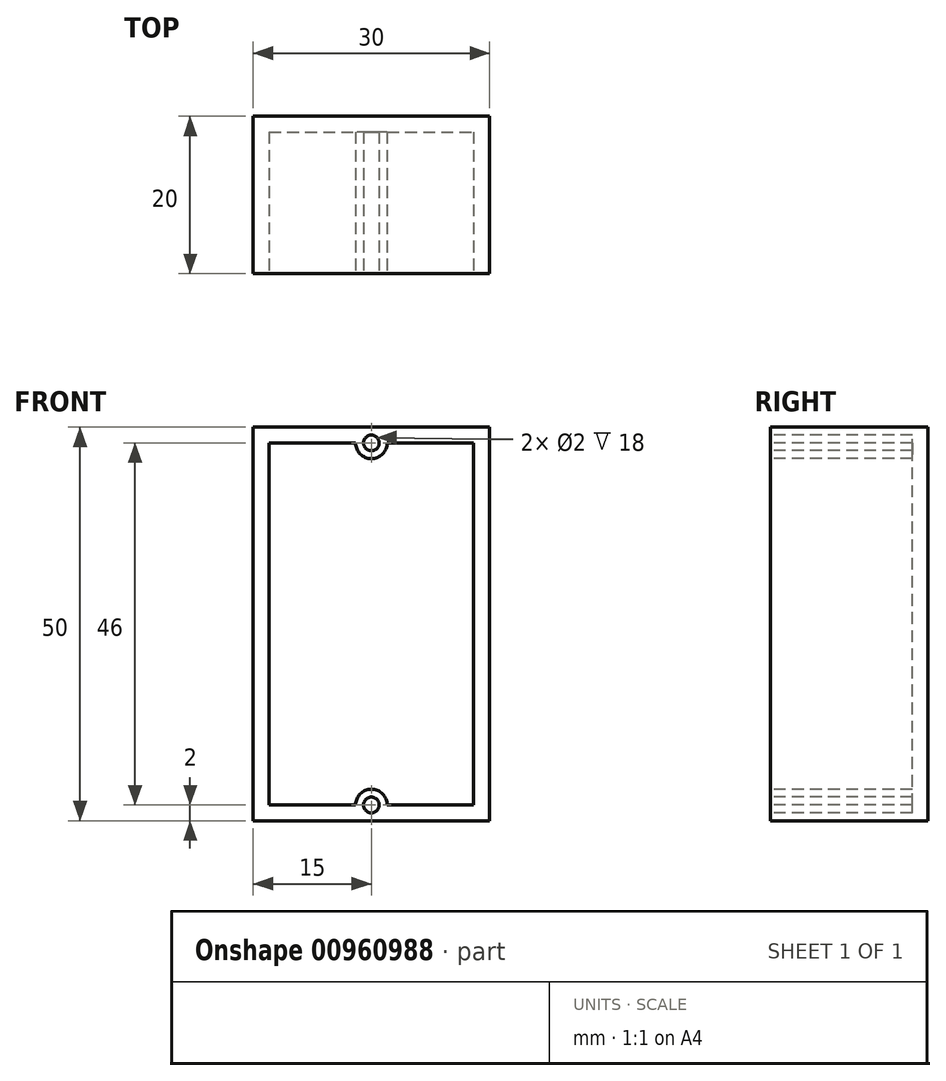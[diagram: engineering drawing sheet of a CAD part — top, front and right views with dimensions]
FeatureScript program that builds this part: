
annotation { "Feature Type Name" : "Feature", "Feature Type Description" : "" }
export const myFeature = defineFeature(function(context is Context, id is Id, definition is map)
    precondition{}
    {
        {
            var Q0;
            Q0=qCreatedBy(makeId("Front.planeOp"),FACE);
            var sketch = newSketch(context, id + "F0", { "sketchPlane" : qUnion([Q0])});
            skLineSegment(sketch, "E0.bottom", {"start": v(0, 0) * mm, "end": v(30, 0) * mm});
            skLineSegment(sketch, "E0.top", {"start": v(0, 50) * mm, "end": v(30, 50) * mm});
            skLineSegment(sketch, "E0.left", {"start": v(0, 0) * mm, "end": v(0, 50) * mm});
            skLineSegment(sketch, "E0.right", {"start": v(30, 0) * mm, "end": v(30, 50) * mm});
            skSolve(sketch);
        }
        {
            var Q0;
            Q0 = qSketchRegion(id + "F0", true);
            extrude(context, id + "F1", {"entities" : qUnion([Q0]), "depth" : 20 * mm, "offsetDistance" : 25 * mm});
        }
        {
            var Q0;
            Q0=makeQuery(id+"F1.opExtrude","CAP_FACE",FACE,{"disambiguationData":[OSD([sQuery(id+"F0.wireOp",EDGE,"E0.bottom"),sQuery(id+"F0.wireOp",EDGE,"E0.top"),sQuery(id+"F0.wireOp",EDGE,"E0.left"),sQuery(id+"F0.wireOp",EDGE,"E0.right")])],"isStart":false});
            cPlane(context, id + "F2", {"entities" : qUnion([Q0]), "cplaneType" : CPlaneType.OFFSET, "offset" : 0 * mm, "width" : 150 * mm, "height" : 150 * mm});
        }
        {
            var Q0;
            Q0=qCreatedBy(id+"F2.planeOp",FACE);
            var sketch = newSketch(context, id + "F3", { "sketchPlane" : qUnion([Q0])});
            skLineSegment(sketch, "E1", {"start": v(0, 0) * mm, "end": v(2, 0) * mm, "construction": true});
            skLineSegment(sketch, "E2", {"start": v(2, 0) * mm, "end": v(2, 2) * mm, "construction": true});
            skLineSegment(sketch, "E3.bottom", {"start": v(2, 2) * mm, "end": v(13, 2) * mm});
            skLineSegment(sketch, "E3.top", {"start": v(2, 48) * mm, "end": v(13, 48) * mm});
            skLineSegment(sketch, "E3.left", {"start": v(2, 2) * mm, "end": v(2, 48) * mm});
            skLineSegment(sketch, "E3.right", {"start": v(28, 2) * mm, "end": v(28, 48) * mm});
            skLineSegment(sketch, "E4", {"start": v(2, 48) * mm, "end": v(13, 48) * mm, "construction": true});
            skLineSegment(sketch, "E5", {"start": v(2, 2) * mm, "end": v(13, 2) * mm, "construction": true});
            skArc(sketch, "E6", {"start": v(17, 2) * mm, "mid": v(15, 4) * mm, "end": v(13, 2) * mm});
            skArc(sketch, "E7", {"start": v(13, 48) * mm, "mid": v(15, 46) * mm, "end": v(17, 48) * mm});
            skLineSegment(sketch, "E8.trimOffspring", {"start": v(17, 48) * mm, "end": v(28, 48) * mm});
            skLineSegment(sketch, "E9.trimOffspring", {"start": v(17, 2) * mm, "end": v(28, 2) * mm});
            skCircle(sketch, "E10", {"center": v(15, 2) * mm, "radius": 1 * mm});
            skCircle(sketch, "E11", {"center": v(15, 48) * mm, "radius": 1 * mm});
            skSolve(sketch);
        }
        {
            var Q0;
            Q0 = qSketchRegion(id + "F3", true);
            extrude(context, id + "F4", {"entities" : qUnion([Q0]), "operationType" : NewBodyOperationType.REMOVE, "oppositeDirection" : true, "depth" : 18 * mm, "offsetDistance" : 25 * mm});
        }
    });
